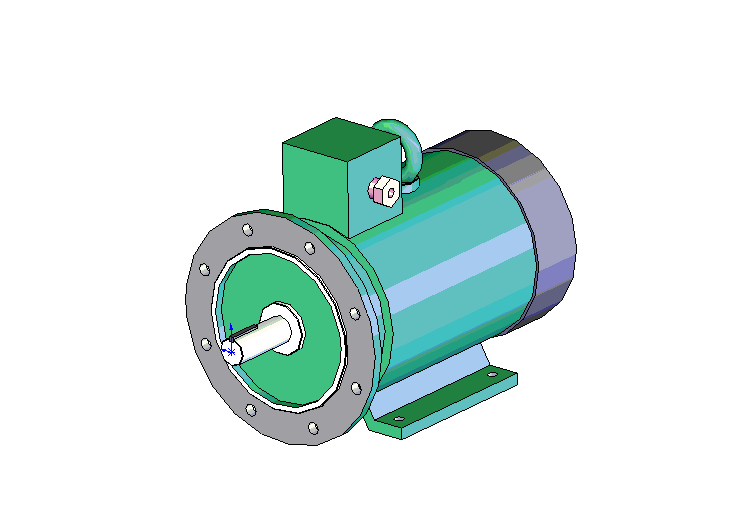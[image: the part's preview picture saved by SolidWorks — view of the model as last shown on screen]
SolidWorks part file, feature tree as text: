
SOLIDWORKS PART (.sldprt)
format: sldprt  version: not decoded by parser v0  size: 714,240 bytes
history: native  units: mm
features: sketch x18, extrude x12, plane x4, cut_extrude x4, chamfer x3, material x1, sweep x1 (+10 scaffold rows collapsed)
feature tree (53):
  scaffold x10  (default folders/planes/origin — collapsed)
  material  "Ст.3 ГОСТ 380-88"
  plane  "Спереди"
  plane  "Сверху"
  plane  "Справа"
  sketch  "Эскиз1"  dims[D1=42.0mm]
  extrude  "Вытянуть1"  Depth=110mm
  sketch  "Эскиз2"  dims[D1=8.0mm D2=8.0mm D3=45.0mm]
  extrude  "Вытянуть2"  Depth=55mm
  sketch  "Эскиз3"  dims[D1=350.0mm]
  extrude  "Вытянуть3"  Depth=15mm
  sketch  "Эскиз4"  dims[D1=250.0mm D2=232.0mm]
  extrude  "Вытянуть4"  Depth=5mm
  sketch  "Эскиз5"  dims[D1=232.0mm D2=80.0mm]
  cut_extrude  "Вырез-Вытянуть1"  Depth=8mm
  chamfer  "Фаска1"  Distance=1mm Angle=45deg
  sketch  "Эскиз6"  dims[c1.D2=19.0mm c1.D1=~222.342459mm c2.D1=22.5deg c2.D3=150.0mm c2.D4=150.0mm c2.D5=150.0mm]
  cut_extrude  "Вырез-Вытянуть2"  [1 undecoded]
  sketch  "Эскиз7"  dims[D1=250.0mm]
  extrude  "Вытянуть5"  Depth=68mm
  sketch  "Эскиз8"  dims[D1=280.0mm]
  extrude  "Вытянуть6"  Depth=322mm
  sketch  "Эскиз9"  dims[D1=288.0mm]
  extrude  "Вытянуть7"  Depth=145mm
  chamfer  "Фаска2"  Distance=60mm Angle=45deg
  sketch  "Эскиз10"  dims[c1.D1=18.0mm c1.D2=18.0mm c1.D3=~100.823354mm c2.D3=30.0deg c2.D4=50.0mm c2.D5=152.0mm c2.D6=160.0mm c2.D7=~105.04342mm]
  extrude  "Вытянуть8"  Depth=260mm
  sketch  "Эскиз11"  dims[c1.D2=15.0mm c1.D1=218.0mm c1.D3=127.0mm c1.D4=90.0deg c1.D5=396.0mm c1.D6=254.0mm c1.D7=178.0mm c2.D5=210.0mm c2.D7=428.0mm]
  cut_extrude  "Вырез-Вытянуть3"  [1 undecoded]
  sketch  "Эскиз12"  dims[D1=120.0mm D2=120.0mm D3=1.0mm]
  extrude  "Вытянуть9"  Depth=245mm
  sketch  "Эскиз13"  dims[D1=70.0mm D2=370.0mm]
  extrude  "Вытянуть10"  Depth=150mm
  chamfer  "Фаска3"  Distance=1mm Angle=45deg
  plane  "Плоскость1"  Offset=370mm
  sketch  "Эскиз14"  dims[D1=76.0mm]
  sketch  "Эскиз15"  dims[D1=24.0mm D2=76.0mm]
  sweep  "По траектории1"
  sketch  "Эскиз16"  dims[D1=32.0mm D2=60.0mm D3=60.0mm]
  extrude  "Вытянуть11"  Depth=14mm
  sketch  "Эскиз17"  dims[D1=19.5mm]
  extrude  "Вытянуть12"  Depth=16mm
  sketch  "Эскиз18"  dims[D1=14.0mm]
  cut_extrude  "Вырез-Вытянуть4"  Depth=16mm
decode coverage: 35 of 38 modeling features carry decoded parameters
note: ~ marks probable driven/reference dimensions
note: 2 parameter values undecoded
note: suppression state not decoded; provenance and decode notes live in map.json
